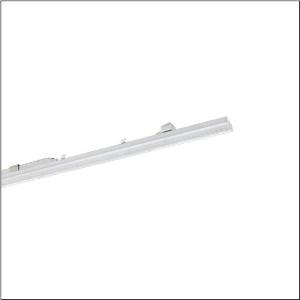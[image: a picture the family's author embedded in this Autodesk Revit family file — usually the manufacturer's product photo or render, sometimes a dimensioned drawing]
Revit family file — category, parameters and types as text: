
# Revit family: tl_l_5wd7a8p0a2b5
name_source: partatom
category: Lighting Fixtures
units: mm (PartAtom-declared; Revit-internal decimal feet)

## family parameters
Cut with Voids When Loaded = No
Host = Face
Light Source = No
Part Type = Normal
Room Calculation Point = No
Round Connector Dimension = Use Diameter
Shared = No

## types (1)
- --- (1 x LED, 5000 lm, 31.5 W, 4000K)
    Apparent Load = 32 VA
    CIE Flux Codes = 49 84 98 100 100
    Color Rendering = 80
    Color Temperature = 4000K
    Default Elevation = 1800 mm
    Description = TL L, luminaire insert, of sheet steel, galvanised, coil coated, white, length: 1.500mm, width: 66mm, height: 67mm, LED light colour: 840, control gear: DALI, with terminal, 5-pole, mains connection: 230..240V, AC, 50/60Hz, rated input power: 63W, primary optical cover: cover, of PMMA, light emission: direct distribution, protection rating (complete): as luminaire, insulation class (complete): insulation class I (protective earthing), certification: CE, impact resistance: IK06, permissible ambient temperature for indoor applications: -35..+35°C, standard: NMF01, packaging unit: 1 piece
    Height = 120 mm
    Lamp = 1 x LED
    Lamp Light Flux = 5000 lm
    Lamp Power = 31.5 W
    Lamp count = 1
    Length = 1690 mm
    Luminous efficacy = 159 lm/W
    Manufacturer = Siteco
    ModVariant = No
    Model = 5WD7A8P0A2B5
    Mounting Place = Ceiling
    Mounting Type = Pendant
    Number of Poles = 1
    OnlyDefault = Yes
    Power Factor = 1
    Product Name = TL L
    Product group = luminaire insert
    ProductGroupID = 901
    Protection Class = Protection class I
    Protection Degree = Degree of protection
    RLX_Detail_Level = 1
    RLX_Emergency_Light_Flux = 0 lm
    RLX_Emergency_Type = 0
    RLX_Emergency_Type_DB = No
    RlxData = <blob elided: 17301 chars, md5=deacb999>
    Socket = socket
    Standby Power = 0 W
    System Light Flux = 5000 lm
    System Power = 32 W
    Type Comments = factory setting: luminous flux: 100 % | dim-lin: 254 | 646 mA
    Type Image = l_1294382.jpg
    URL = http://relux.com
    VarID = @adj_016925
    Voltage = 0 V
    Weight = 0.00 kg
    Width = 208 mm

## geometry (parser evidence)
native form markers: Blend x4, Sweep x12
no freeform markers — native parametric forms only
